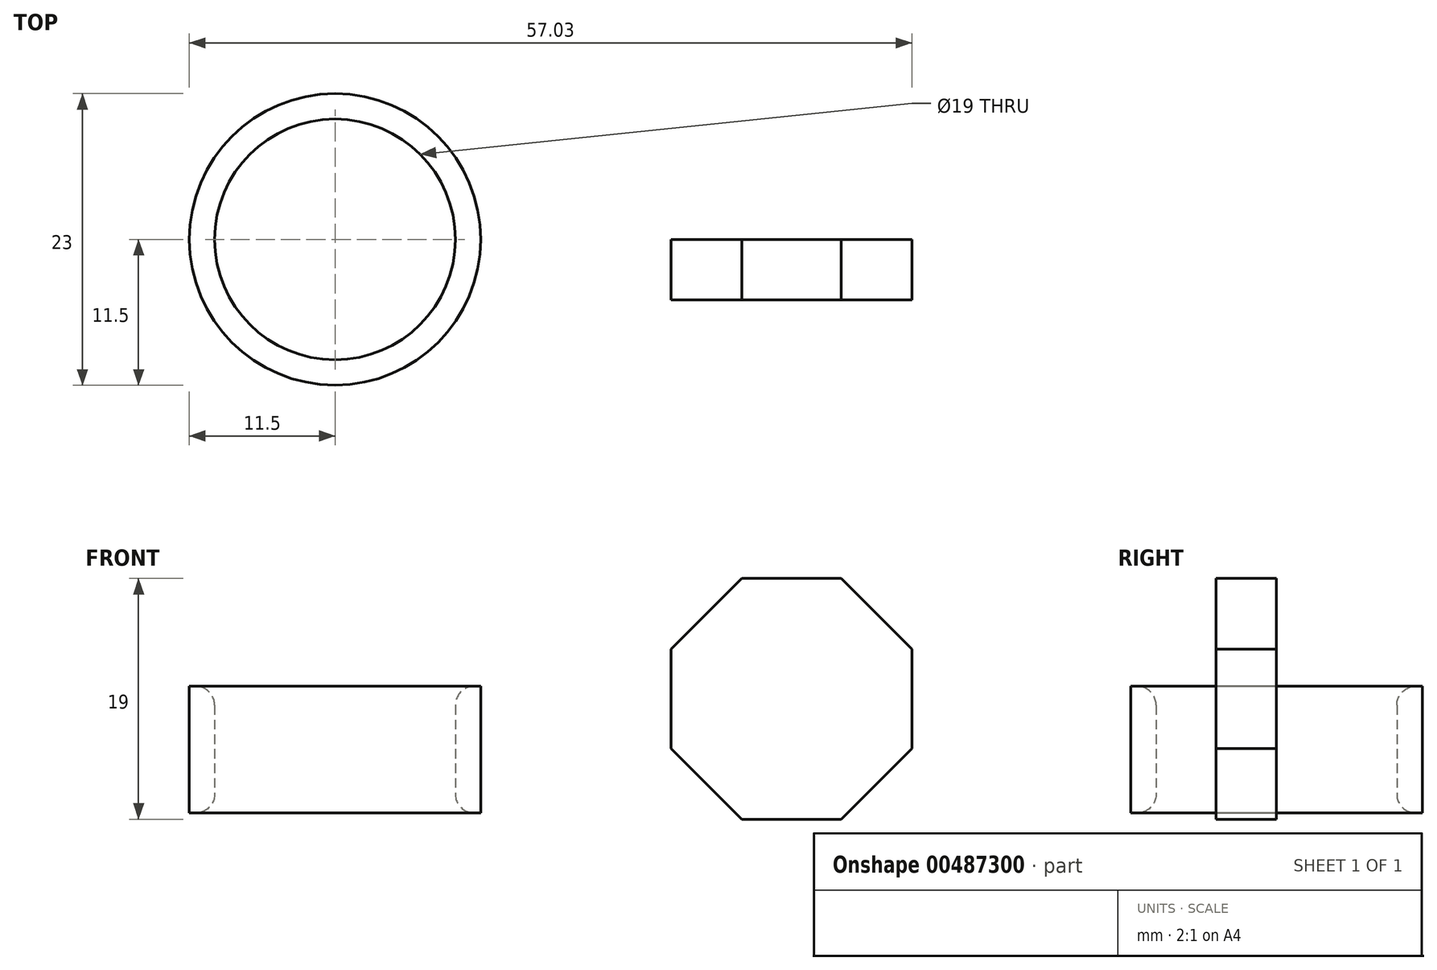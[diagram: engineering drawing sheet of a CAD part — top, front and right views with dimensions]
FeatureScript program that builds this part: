
annotation { "Feature Type Name" : "Feature", "Feature Type Description" : "" }
export const myFeature = defineFeature(function(context is Context, id is Id, definition is map)
    precondition{}
    {
        {
            var Q0;
            Q0=qCreatedBy(makeId("Top.planeOp"),FACE);
            var sketch = newSketch(context, id + "F0", { "sketchPlane" : qUnion([Q0])});
            skCircle(sketch, "E0", {"center": v(0, 0) * mm, "radius": 9.5 * mm});
            skCircle(sketch, "E1", {"center": v(0, 0) * mm, "radius": 11.5 * mm});
            skSolve(sketch);
        }
        {
            var Q0;
            Q0=makeQuery(id+"F0.imprint","IMPRINT",FACE,{"disambiguationData":[TD([[makeQuery(id+"F0.imprint","IMPRINT",EDGE,{"derivedFrom":sQuery(id+"F0.wireOp",EDGE,"E0")}),-1.0]])]});
            extrude(context, id + "F1", {"entities" : qUnion([Q0]), "depth" : 10 * mm});
        }
        {
            var Q0;
            Q0=makeQuery(id+"F1.opExtrude","CAP_EDGE",EDGE,{"disambiguationData":[OSD([sQuery(id+"F0.wireOp",EDGE,"E0")])],"isStart":false});
            var Q1;
            Q1=makeQuery(id+"F1.opExtrude","CAP_EDGE",EDGE,{"disambiguationData":[OSD([sQuery(id+"F0.wireOp",EDGE,"E0")])],"isStart":true});
            fillet(context, id + "F2", {"entities" : qUnion([Q0, Q1]), "radius" : 1.5 * mm, "tangentPropagation" : true, "allowEdgeOverflow" : false});
        }
        {
            var Q0;
            Q0=qCreatedBy(makeId("Front.planeOp"),FACE);
            var sketch = newSketch(context, id + "F3", { "sketchPlane" : qUnion([Q0])});
            skCircle(sketch, "E2.cCircle", {"center": v(36.03, 9) * mm, "radius": 9.5 * mm, "construction": true});
            skLineSegment(sketch, "E2.0", {"start": v(32.1, 18.5) * mm, "end": v(39.97, 18.5) * mm});
            skLineSegment(sketch, "E2.1", {"start": v(39.97, 18.5) * mm, "end": v(45.53, 12.94) * mm});
            skLineSegment(sketch, "E2.2", {"start": v(45.53, 12.94) * mm, "end": v(45.53, 5.07) * mm});
            skLineSegment(sketch, "E2.3", {"start": v(45.53, 5.07) * mm, "end": v(39.97, -0.5) * mm});
            skLineSegment(sketch, "E2.4", {"start": v(39.97, -0.5) * mm, "end": v(32.1, -0.5) * mm});
            skLineSegment(sketch, "E2.5", {"start": v(32.1, -0.5) * mm, "end": v(26.53, 5.07) * mm});
            skLineSegment(sketch, "E2.6", {"start": v(26.53, 5.07) * mm, "end": v(26.53, 12.94) * mm});
            skLineSegment(sketch, "E2.7", {"start": v(26.53, 12.94) * mm, "end": v(32.1, 18.5) * mm});
            skPoint(sketch, "E2.0.midPoint", {"position": v(36.03, 18.5) * mm});
            skSolve(sketch);
        }
        {
            var Q0;
            Q0=makeQuery(id+"F3.imprint","IMPRINT",FACE,{"disambiguationData":[TD([[makeQuery(id+"F3.imprint","IMPRINT",EDGE,{"derivedFrom":sQuery(id+"F3.wireOp",EDGE,"E2.0")}),-1.0]])]});
            extrude(context, id + "F4", {"entities" : qUnion([Q0]), "depth" : 4.76 * mm});
        }
    });
